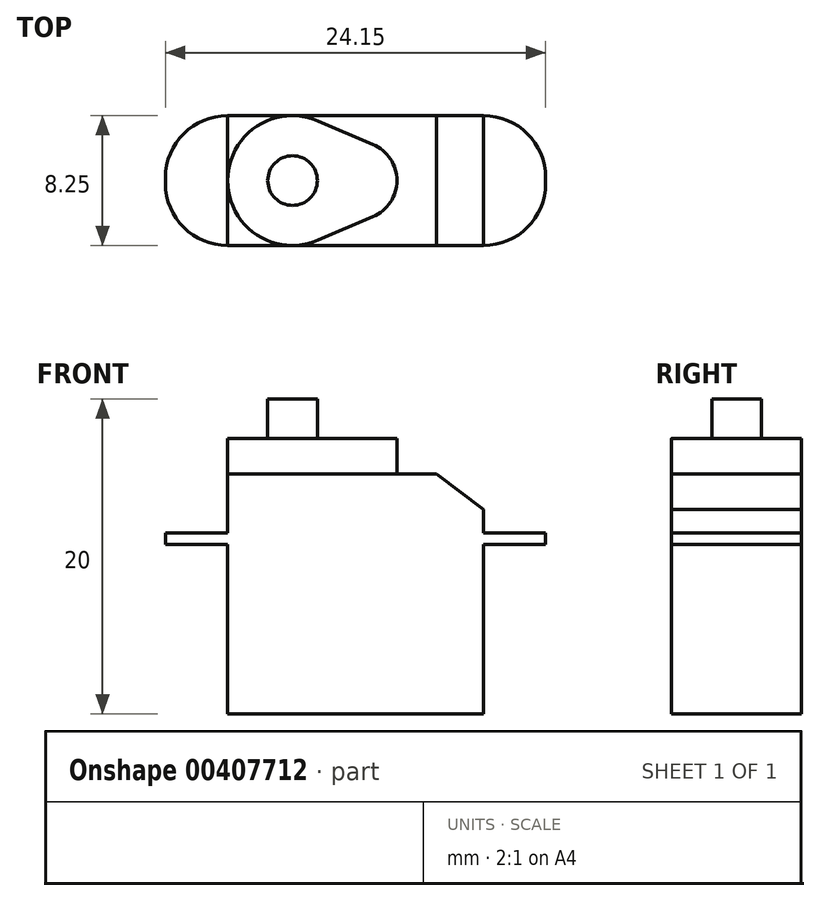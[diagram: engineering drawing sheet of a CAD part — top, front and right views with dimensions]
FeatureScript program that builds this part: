
annotation { "Feature Type Name" : "Feature", "Feature Type Description" : "" }
export const myFeature = defineFeature(function(context is Context, id is Id, definition is map)
    precondition{}
    {
        {
            var Q0;
            Q0=qCreatedBy(makeId("Front.planeOp"),FACE);
            var sketch = newSketch(context, id + "F0", { "sketchPlane" : qUnion([Q0])});
            skLineSegment(sketch, "E0.bottom", {"start": v(0, 0) * mm, "end": v(16.25, 0) * mm});
            skLineSegment(sketch, "E0.top", {"start": v(10.75, 15.25) * mm, "end": v(13.25, 15.25) * mm});
            skLineSegment(sketch, "E0.left", {"start": v(0, 0) * mm, "end": v(0, 10.75) * mm});
            skLineSegment(sketch, "E0.right", {"start": v(16.25, 0) * mm, "end": v(16.25, 10.75) * mm});
            skLineSegment(sketch, "E1", {"start": v(0, 17.5) * mm, "end": v(10.75, 17.5) * mm});
            skLineSegment(sketch, "E2", {"start": v(10.75, 17.5) * mm, "end": v(10.75, 15.25) * mm});
            skLineSegment(sketch, "E3", {"start": v(13.25, 15.25) * mm, "end": v(16.25, 13) * mm});
            skLineSegment(sketch, "E4", {"start": v(16.25, 11.5) * mm, "end": v(20.2, 11.5) * mm});
            skLineSegment(sketch, "E5", {"start": v(20.2, 11.5) * mm, "end": v(20.2, 10.75) * mm});
            skLineSegment(sketch, "E6", {"start": v(20.2, 10.75) * mm, "end": v(16.25, 10.75) * mm});
            skLineSegment(sketch, "E7", {"start": v(0, 11.5) * mm, "end": v(-3.95, 11.5) * mm});
            skLineSegment(sketch, "E8", {"start": v(-3.95, 11.5) * mm, "end": v(-3.95, 10.75) * mm});
            skLineSegment(sketch, "E9", {"start": v(-3.95, 10.75) * mm, "end": v(0, 10.75) * mm});
            skLineSegment(sketch, "E10.trimOffspring", {"start": v(16.25, 11.5) * mm, "end": v(16.25, 13) * mm});
            skLineSegment(sketch, "E11", {"start": v(0, 11.5) * mm, "end": v(0, 17.5) * mm});
            skSolve(sketch);
        }
        {
            var Q0;
            Q0 = qSketchRegion(id + "F0", true);
            extrude(context, id + "F1", {"entities" : qUnion([Q0]), "depth" : 8.25 * mm});
        }
        {
            var Q0;
            Q0=makeQuery(id+"F1.opExtrude","SWEPT_FACE",FACE,{"disambiguationData":[OSD([sQuery(id+"F0.wireOp",EDGE,"E7")])]});
            var sketch = newSketch(context, id + "F2", { "sketchPlane" : qUnion([Q0])});
            skArc(sketch, "E12", {"start": v(-3.95, -4.3) * mm, "mid": v(-2.8, -7.1) * mm, "end": v(0, -8.25) * mm});
            skArc(sketch, "E13", {"start": v(0, 0) * mm, "mid": v(-2.8, -1.16) * mm, "end": v(-3.95, -3.95) * mm});
            skLineSegment(sketch, "E14", {"start": v(-3.95, 0) * mm, "end": v(20.2, 0) * mm, "construction": true});
            skLineSegment(sketch, "E15", {"start": v(8.12, 0) * mm, "end": v(8.12, -8.25) * mm, "construction": true});
            skLineSegment(sketch, "E16.MirrorCS", {"start": v(20.2, 0) * mm, "end": v(-3.95, 0) * mm, "construction": true});
            skArc(sketch, "E17.MirrorCS", {"start": v(16.25, 0) * mm, "mid": v(19.04, -1.16) * mm, "end": v(20.2, -3.95) * mm});
            skArc(sketch, "E18.MirrorCS", {"start": v(20.2, -4.3) * mm, "mid": v(19.04, -7.1) * mm, "end": v(16.25, -8.25) * mm});
            skLineSegment(sketch, "E19", {"start": v(-3.95, 0) * mm, "end": v(0, 0) * mm});
            skLineSegment(sketch, "E20", {"start": v(16.25, 0) * mm, "end": v(20.2, 0) * mm});
            skLineSegment(sketch, "E21", {"start": v(20.2, -3.95) * mm, "end": v(20.2, 0) * mm});
            skLineSegment(sketch, "E22", {"start": v(20.2, -4.3) * mm, "end": v(20.2, -8.25) * mm});
            skLineSegment(sketch, "E23", {"start": v(20.2, -8.25) * mm, "end": v(16.25, -8.25) * mm});
            skLineSegment(sketch, "E24", {"start": v(-3.95, 0) * mm, "end": v(-3.95, -3.95) * mm});
            skLineSegment(sketch, "E25", {"start": v(-3.95, -4.3) * mm, "end": v(-3.95, -8.25) * mm});
            skLineSegment(sketch, "E26", {"start": v(-3.95, -8.25) * mm, "end": v(0, -8.25) * mm});
            skSolve(sketch);
        }
        {
            var Q0;
            Q0 = qSketchRegion(id + "F2", true);
            var Q1;
            Q1=makeQuery(id+"F1.opExtrude","SWEPT_FACE",FACE,{"disambiguationData":[OSD([sQuery(id+"F0.wireOp",EDGE,"E9")])]});
            extrude(context, id + "F3", {"entities" : qUnion([Q0]), "operationType" : NewBodyOperationType.REMOVE, "endBound" : BoundingType.UP_TO_SURFACE, "oppositeDirection" : true, "endBoundEntityFace" : qUnion([Q1]), "depth" : 25 * mm});
        }
        {
            var Q0;
            Q0=makeQuery(id+"F1.opExtrude","SWEPT_FACE",FACE,{"disambiguationData":[OSD([sQuery(id+"F0.wireOp",EDGE,"E1")])]});
            var sketch = newSketch(context, id + "F4", { "sketchPlane" : qUnion([Q0])});
            skArc(sketch, "E27", {"start": v(5.75, -0.33) * mm, "mid": v(0, -4.12) * mm, "end": v(5.75, -7.92) * mm});
            skLineSegment(sketch, "E28", {"start": v(0, -8.25) * mm, "end": v(4.12, -8.25) * mm});
            skLineSegment(sketch, "E29", {"start": v(0, -8.25) * mm, "end": v(0, -4.12) * mm});
            skLineSegment(sketch, "E30", {"start": v(0, -4.12) * mm, "end": v(0, 0) * mm});
            skLineSegment(sketch, "E31", {"start": v(0, 0) * mm, "end": v(4.12, 0) * mm});
            skArc(sketch, "E32", {"start": v(9.23, -6.42) * mm, "mid": v(10.75, -4.12) * mm, "end": v(9.23, -1.83) * mm});
            skLineSegment(sketch, "E33", {"start": v(5.75, -0.33) * mm, "end": v(9.23, -1.83) * mm});
            skLineSegment(sketch, "E34", {"start": v(5.75, -7.92) * mm, "end": v(9.23, -6.42) * mm});
            skLineSegment(sketch, "E35", {"start": v(4.12, 0) * mm, "end": v(10.75, 0) * mm});
            skLineSegment(sketch, "E36", {"start": v(10.75, 0) * mm, "end": v(10.75, -4.12) * mm});
            skLineSegment(sketch, "E37", {"start": v(10.75, -4.12) * mm, "end": v(10.75, -8.25) * mm});
            skLineSegment(sketch, "E38", {"start": v(10.75, -8.25) * mm, "end": v(4.12, -8.25) * mm});
            skSolve(sketch);
        }
        {
            var Q0;
            {var subQ0=sQuery(id+"F4.wireOp",EDGE,"E28");Q0=makeQuery(id+"F4.imprint","IMPRINT",FACE,{"disambiguationData":[TD([[makeQuery(id+"F4.imprint","IMPRINT",EDGE,{"derivedFrom":subQ0}),1.0]])]});}
            var Q1;
            {var subQ2=sQuery(id+"F4.wireOp",EDGE,"E31");Q1=makeQuery(id+"F4.imprint","IMPRINT",FACE,{"disambiguationData":[TD([[makeQuery(id+"F4.imprint","IMPRINT",EDGE,{"derivedFrom":subQ2}),-1.0]])]});}
            var Q2;
            {var subQ1=sQuery(id+"F4.wireOp",EDGE,"E33");Q2=makeQuery(id+"F4.imprint","IMPRINT",FACE,{"disambiguationData":[TD([[makeQuery(id+"F4.imprint","IMPRINT",EDGE,{"derivedFrom":subQ1}),1.0]])]});}
            var Q3;
            {var subQ1=sQuery(id+"F4.wireOp",EDGE,"E34");Q3=makeQuery(id+"F4.imprint","IMPRINT",FACE,{"disambiguationData":[TD([[makeQuery(id+"F4.imprint","IMPRINT",EDGE,{"derivedFrom":subQ1}),-1.0]])]});}
            var Q4;
            Q4=makeQuery(id+"F1.opExtrude","SWEPT_FACE",FACE,{"disambiguationData":[OSD([sQuery(id+"F0.wireOp",EDGE,"E0.top")])]});
            extrude(context, id + "F5", {"entities" : qUnion([Q0, Q1, Q2, Q3]), "operationType" : NewBodyOperationType.REMOVE, "endBound" : BoundingType.UP_TO_SURFACE, "oppositeDirection" : true, "endBoundEntityFace" : qUnion([Q4]), "depth" : 25 * mm});
        }
        {
            var Q0;
            Q0=makeQuery(id+"F1.opExtrude","SWEPT_FACE",FACE,{"disambiguationData":[OSD([sQuery(id+"F0.wireOp",EDGE,"E1")])]});
            var sketch = newSketch(context, id + "F6", { "sketchPlane" : qUnion([Q0])});
            skCircle(sketch, "E39", {"center": v(4.12, -4.12) * mm, "radius": 1.57 * mm});
            skSolve(sketch);
        }
        {
            var Q0;
            Q0 = qSketchRegion(id + "F6", true);
            extrude(context, id + "F7", {"entities" : qUnion([Q0]), "depth" : 2.5 * mm});
        }
    });
